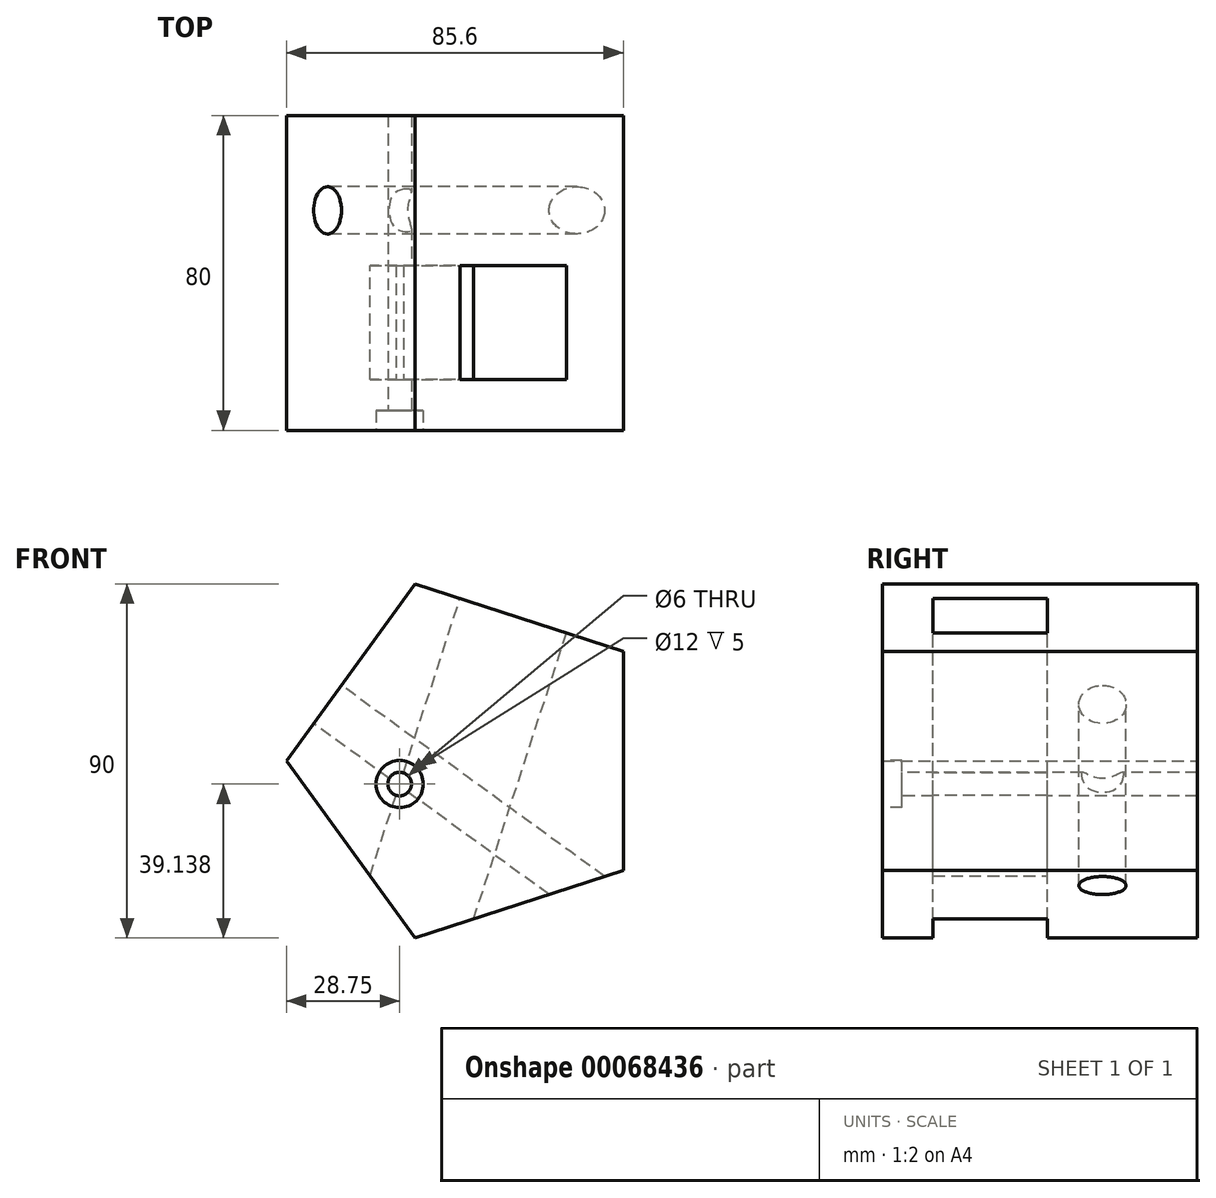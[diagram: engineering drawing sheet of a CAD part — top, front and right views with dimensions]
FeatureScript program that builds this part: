
annotation { "Feature Type Name" : "Feature", "Feature Type Description" : "" }
export const myFeature = defineFeature(function(context is Context, id is Id, definition is map)
    precondition{}
    {
        {
            var Q0;
            Q0=qCreatedBy(makeId("Front.planeOp"),FACE);
            var sketch = newSketch(context, id + "F0", { "sketchPlane" : qUnion([Q0])});
            skCircle(sketch, "E0.cCircle", {"center": v(-38.28, 0) * mm, "radius": 38.28 * mm, "construction": true});
            skLineSegment(sketch, "E0.0", {"start": v(0, 27.81) * mm, "end": v(0, -27.81) * mm});
            skLineSegment(sketch, "E0.1", {"start": v(0, -27.81) * mm, "end": v(-52.9, -45) * mm});
            skLineSegment(sketch, "E0.2", {"start": v(-52.9, -45) * mm, "end": v(-85.6, 0) * mm});
            skLineSegment(sketch, "E0.3", {"start": v(-85.6, 0) * mm, "end": v(-52.9, 45) * mm});
            skLineSegment(sketch, "E0.4", {"start": v(-52.9, 45) * mm, "end": v(0, 27.81) * mm});
            skPoint(sketch, "E0.0.midPoint", {"position": v(0, 0) * mm});
            skSolve(sketch);
        }
        {
            var Q0;
            Q0=makeQuery(id+"F0.imprint","IMPRINT",FACE,{"disambiguationData":[TD([[makeQuery(id+"F0.imprint","IMPRINT",EDGE,{"derivedFrom":sQuery(id+"F0.wireOp",EDGE,"E0.0")}),-1.0]])]});
            extrude(context, id + "F1", {"entities" : qUnion([Q0]), "depth" : 80 * mm});
        }
        {
            var Q0;
            Q0=makeQuery(id+"F1.opExtrude","CAP_FACE",FACE,{"disambiguationData":[OSD([sQuery(id+"F0.wireOp",EDGE,"E0.0"),sQuery(id+"F0.wireOp",EDGE,"E0.1"),sQuery(id+"F0.wireOp",EDGE,"E0.2"),sQuery(id+"F0.wireOp",EDGE,"E0.3"),sQuery(id+"F0.wireOp",EDGE,"E0.4")])],"isStart":false});
            var sketch = newSketch(context, id + "F2", { "sketchPlane" : qUnion([Q0])});
            skPoint(sketch, "E1", {"position": v(-56.85, -5.86) * mm});
            skSolve(sketch);
        }
        {
            var Q0;
            Q0=sQuery(id+"F2.wireOp",VERTEX,"E1");
            var Q1;
            Q1=makeQuery(id+"F1.opExtrude","SWEPT_BODY",BODY,{"disambiguationData":[OSD([sQuery(id+"F0.wireOp",EDGE,"E0.0"),sQuery(id+"F0.wireOp",EDGE,"E0.1"),sQuery(id+"F0.wireOp",EDGE,"E0.2"),sQuery(id+"F0.wireOp",EDGE,"E0.3"),sQuery(id+"F0.wireOp",EDGE,"E0.4")])]});
            hole(context, id + "F3", {"style" : HoleStyle.C_BORE, "holeDiameter" : 6 * mm, "cBoreDiameter" : 12 * mm, "cBoreDepth" : 5 * mm, "endStyle" : HoleEndStyle.THROUGH, "locations" : qUnion([Q0]), "scope" : qUnion([Q1])});
        }
        {
            var Q0;
            Q0=makeQuery(id+"F1.opExtrude","SWEPT_FACE",FACE,{"disambiguationData":[OSD([sQuery(id+"F0.wireOp",EDGE,"E0.3")])]});
            var sketch = newSketch(context, id + "F4", { "sketchPlane" : qUnion([Q0])});
            skPoint(sketch, "E2", {"position": v(24.09, -32.57) * mm});
            skSolve(sketch);
        }
        {
            var Q0;
            Q0=sQuery(id+"F4.wireOp",VERTEX,"E2");
            var Q1;
            Q1=makeQuery(id+"F1.opExtrude","SWEPT_BODY",BODY,{"disambiguationData":[OSD([sQuery(id+"F0.wireOp",EDGE,"E0.0"),sQuery(id+"F0.wireOp",EDGE,"E0.1"),sQuery(id+"F0.wireOp",EDGE,"E0.2"),sQuery(id+"F0.wireOp",EDGE,"E0.3"),sQuery(id+"F0.wireOp",EDGE,"E0.4")])]});
            hole(context, id + "F5", {"style" : HoleStyle.SIMPLE, "holeDiameter" : 12 * mm, "endStyle" : HoleEndStyle.THROUGH, "locations" : qUnion([Q0]), "scope" : qUnion([Q1])});
        }
        {
            var Q0;
            Q0=makeQuery(id+"F1.opExtrude","SWEPT_FACE",FACE,{"disambiguationData":[OSD([sQuery(id+"F0.wireOp",EDGE,"E0.4")])]});
            var sketch = newSketch(context, id + "F6", { "sketchPlane" : qUnion([Q0])});
            skCircle(sketch, "E3", {"center": v(-41.1, -28.12) * mm, "radius": 12.2 * mm});
            skLineSegment(sketch, "E4.bottom", {"start": v(-52.25, -38.1) * mm, "end": v(-23.8, -38.1) * mm});
            skLineSegment(sketch, "E4.top", {"start": v(-52.25, -67.13) * mm, "end": v(-23.8, -67.13) * mm});
            skLineSegment(sketch, "E4.left", {"start": v(-52.25, -38.1) * mm, "end": v(-52.25, -67.13) * mm});
            skLineSegment(sketch, "E4.right", {"start": v(-23.8, -38.1) * mm, "end": v(-23.8, -67.13) * mm});
            skSolve(sketch);
        }
        {
            var Q0;
            {var subQ0=sQuery(id+"F6.wireOp",EDGE,"E4.bottom");var subQ1=sQuery(id+"F6.wireOp",EDGE,"E3");var subQ2=makeQuery(id+"F6.imprint","INTERSECT",VERTEX,{"disambiguationData":[OD(0.0)],"derivedFrom":[subQ1,subQ0]});Q0=makeQuery(id+"F6.imprint","IMPRINT",FACE,{"disambiguationData":[TD([[makeQuery(id+"F6.imprint","IMPRINT",EDGE,{"disambiguationData":[TD([[subQ2,1.0]])],"derivedFrom":subQ1}),1.0]])]});}
            var Q1;
            Q1=makeQuery(id+"F6.imprint","IMPRINT",FACE,{"disambiguationData":[TD([[makeQuery(id+"F6.imprint","IMPRINT",EDGE,{"derivedFrom":sQuery(id+"F6.wireOp",EDGE,"E4.top")}),1.0]])]});
            extrude(context, id + "F7", {"entities" : qUnion([Q0, Q1]), "operationType" : NewBodyOperationType.REMOVE, "oppositeDirection" : true, "depth" : 166.21 * mm});
        }
    });
